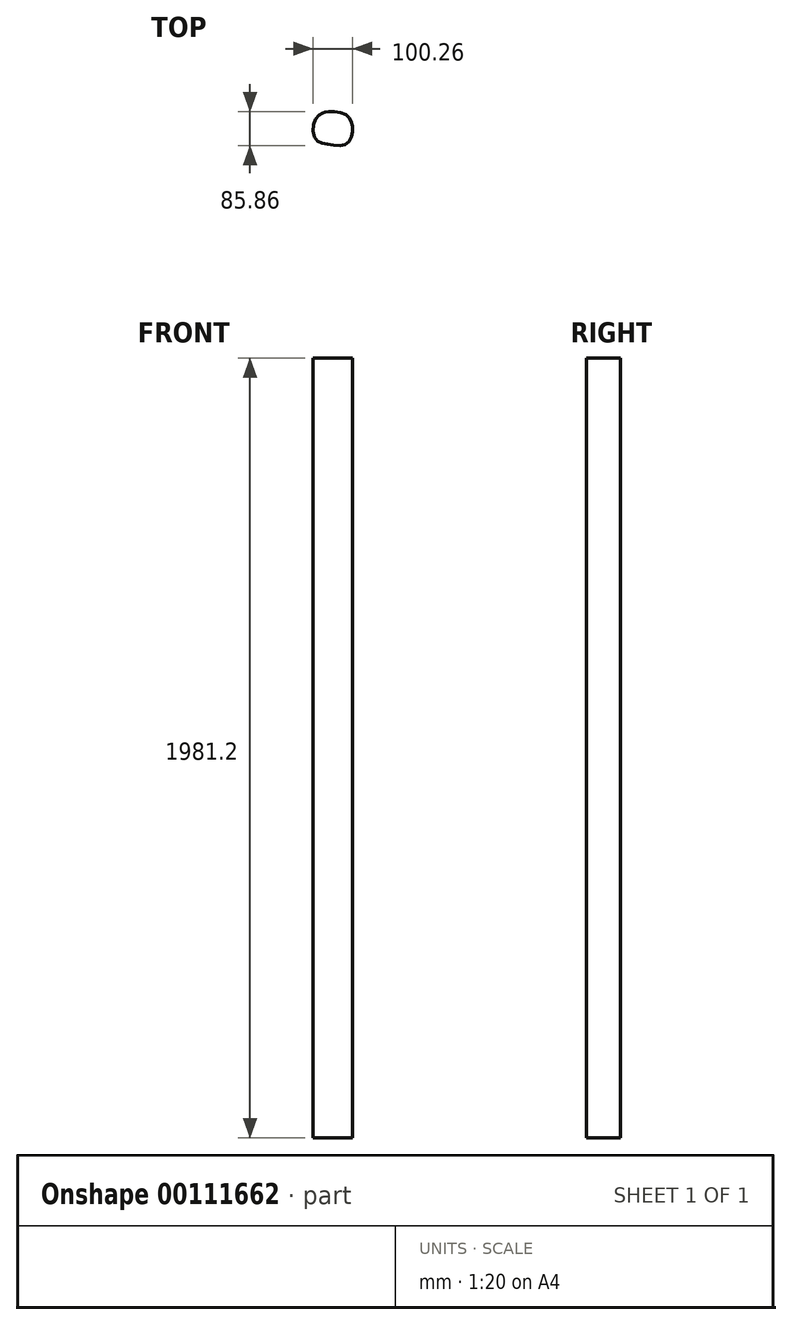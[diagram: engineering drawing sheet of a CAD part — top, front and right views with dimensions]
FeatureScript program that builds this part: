
annotation { "Feature Type Name" : "Feature", "Feature Type Description" : "" }
export const myFeature = defineFeature(function(context is Context, id is Id, definition is map)
    precondition{}
    {
        {
            var Q0;
            Q0=qCreatedBy(makeId("Top.planeOp"),FACE);
            var sketch = newSketch(context, id + "F0", { "sketchPlane" : qUnion([Q0])});
            skFitSpline(sketch, "E0", {"points": [v(-28.28, 41.29) * mm, v(-47.9, 22) * mm, v(-44.76, -24.81) * mm, v(-13.76, -37.47) * mm, v(30.54, -38.1) * mm, v(47.63, -9.96) * mm, v(44.16, 23.25) * mm, v(24.87, 40.65) * mm, v(-17.84, 44.45) * mm, v(-28.28, 41.29) * mm]});
            skSolve(sketch);
        }
        {
            var Q0;
            Q0=makeQuery(id+"F0.imprint","IMPRINT",FACE,{"disambiguationData":[TD([[makeQuery(id+"F0.imprint","IMPRINT",EDGE,{"derivedFrom":sQuery(id+"F0.wireOp",EDGE,"E0")}),1.0]])]});
            extrude(context, id + "F1", {"entities" : qUnion([Q0]), "depth" : 1981.2 * mm});
        }
    });
